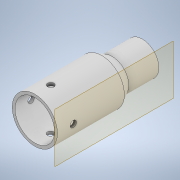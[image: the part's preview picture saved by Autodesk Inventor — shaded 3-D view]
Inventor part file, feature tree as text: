
AUTODESK INVENTOR PART (.ipt)
format: ipt  version: 2021 (Build 250183000, 183)  size: 149,504 bytes
history: native  units: in
note: dims shown in document units (in); Inventor stores cm internally (conversion verified against a paired STEP export)
features: sketch x2, revolve x1, plane x1, extrude x1, pattern_circular x1
ambient origin geometry x8: Origin, YZ Plane, XZ Plane, XY Plane, X Axis, Y Axis, Z Axis, Center Point
bodies: Solid1 (feature_tree)
feature tree (6):
  revolve  "Revolution1"  [1 undecoded]
  plane  "Work Plane1"
  extrude  "Extrusion1"  Depth=0.3937in
  pattern_circular  "Circular Pattern1"  [2 undecoded]
  sketch  "Sketch1"  dims[d5=0.2441in d6=0.1693in]
  sketch  "Sketch2"  dims[d7=0.0354in d8=0.0354in d9=0.0354in d10=0.8189in d11=0.3819in d12=150.0deg d13=90.0deg d14=0.315in d15=0.1969in d16=0.0787in d17=0.3937in d18=0.0in d19=1.5748in d20=360.0deg]
note: 3 required parameter values undecoded (feature->parameter linkage not recoverable at this tier; creation-order binding heuristic only, values carry confidence <= 0.55)